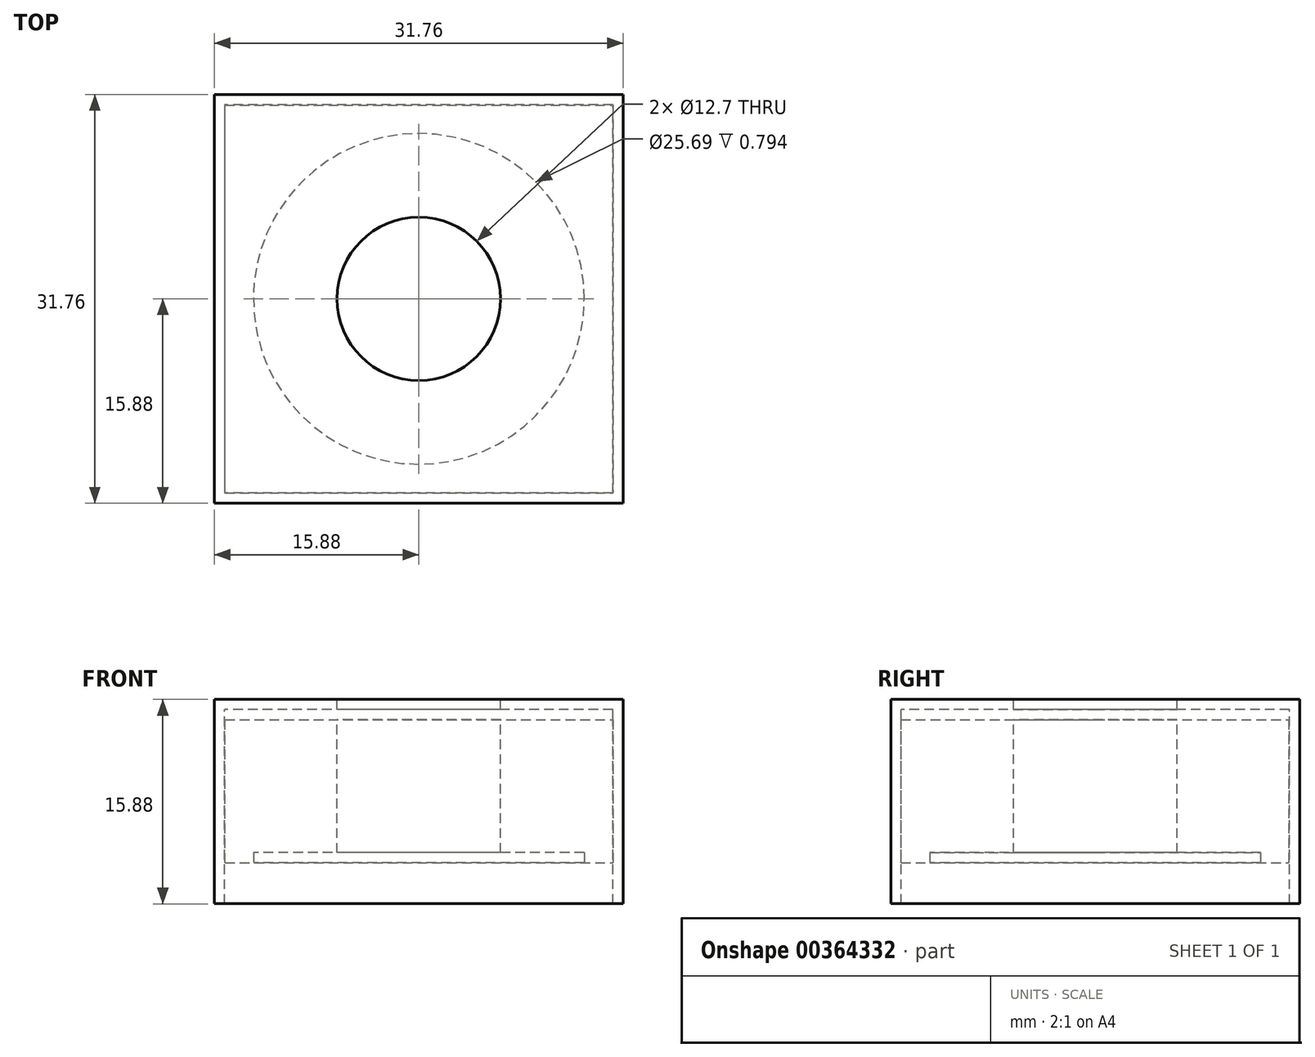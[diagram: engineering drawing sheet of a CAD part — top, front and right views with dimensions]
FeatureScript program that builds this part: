
annotation { "Feature Type Name" : "Feature", "Feature Type Description" : "" }
export const myFeature = defineFeature(function(context is Context, id is Id, definition is map)
    precondition{}
    {
        {
            var Q0;
            Q0=qCreatedBy(makeId("Top.planeOp"),FACE);
            var sketch = newSketch(context, id + "F0", { "sketchPlane" : qUnion([Q0])});
            skLineSegment(sketch, "E0.bottom", {"start": v(15.87, 15.88) * mm, "end": v(-15.88, 15.88) * mm});
            skLineSegment(sketch, "E0.top", {"start": v(15.88, -15.87) * mm, "end": v(-15.87, -15.87) * mm});
            skLineSegment(sketch, "E0.left", {"start": v(15.87, 15.88) * mm, "end": v(15.88, -15.87) * mm});
            skLineSegment(sketch, "E0.right", {"start": v(-15.88, 15.88) * mm, "end": v(-15.87, -15.87) * mm});
            skPoint(sketch, "E0.middle", {"position": v(0, 0) * mm});
            skSolve(sketch);
        }
        {
            var Q0;
            Q0 = qSketchRegion(id + "F0", true);
            extrude(context, id + "F1", {"entities" : qUnion([Q0]), "oppositeDirection" : true, "depth" : 15.88 * mm});
        }
        {
            var Q0;
            Q0=makeQuery(id+"F1.opExtrude","CAP_FACE",FACE,{"disambiguationData":[OSD([sQuery(id+"F0.wireOp",EDGE,"E0.bottom"),sQuery(id+"F0.wireOp",EDGE,"E0.top"),sQuery(id+"F0.wireOp",EDGE,"E0.left"),sQuery(id+"F0.wireOp",EDGE,"E0.right")])],"isStart":false});
            shell(context, id + "F2", {"entities" : qUnion([Q0]), "thickness" : 0.8 * mm});
        }
        {
            var Q0;
            Q0=qCreatedBy(makeId("Top.planeOp"),FACE);
            cPlane(context, id + "F3", {"entities" : qUnion([Q0]), "cplaneType" : CPlaneType.OFFSET, "offset" : 12.7 * mm, "oppositeDirection" : true, "width" : 152.4 * mm, "height" : 152.4 * mm});
        }
        {
            var Q0;
            Q0=qCreatedBy(id+"F3.planeOp",FACE);
            var sketch = newSketch(context, id + "F4", { "sketchPlane" : qUnion([Q0])});
            skLineSegment(sketch, "E1.bottom", {"start": v(-15.05, -15.08) * mm, "end": v(15.17, -15.08) * mm});
            skLineSegment(sketch, "E1.top", {"start": v(-15.05, 15.04) * mm, "end": v(15.17, 15.04) * mm});
            skLineSegment(sketch, "E1.left", {"start": v(-15.05, -15.08) * mm, "end": v(-15.05, 15.04) * mm});
            skLineSegment(sketch, "E1.right", {"start": v(15.17, -15.08) * mm, "end": v(15.17, 15.04) * mm});
            skSolve(sketch);
        }
        {
            var Q0;
            Q0 = qSketchRegion(id + "F4", true);
            extrude(context, id + "F5", {"entities" : qUnion([Q0]), "operationType" : NewBodyOperationType.ADD, "depth" : 11.1 * mm});
        }
        {
            var Q0;
            Q0=makeQuery(id+"F1.opExtrude","CAP_FACE",FACE,{"disambiguationData":[OSD([sQuery(id+"F0.wireOp",EDGE,"E0.bottom"),sQuery(id+"F0.wireOp",EDGE,"E0.top"),sQuery(id+"F0.wireOp",EDGE,"E0.left"),sQuery(id+"F0.wireOp",EDGE,"E0.right")])],"isStart":true});
            var sketch = newSketch(context, id + "F6", { "sketchPlane" : qUnion([Q0])});
            skCircle(sketch, "E2", {"center": v(0, 0) * mm, "radius": 6.35 * mm});
            skSolve(sketch);
        }
        {
            var Q0;
            Q0 = qSketchRegion(id + "F6", true);
            extrude(context, id + "F7", {"entities" : qUnion([Q0]), "operationType" : NewBodyOperationType.REMOVE, "endBound" : BoundingType.THROUGH_ALL, "oppositeDirection" : true, "depth" : 25.4 * mm});
        }
        {
            var Q0;
            Q0=qCreatedBy(id+"F3.planeOp",FACE);
            var sketch = newSketch(context, id + "F8", { "sketchPlane" : qUnion([Q0])});
            skCircle(sketch, "E3", {"center": v(0, 0) * mm, "radius": 12.85 * mm});
            skSolve(sketch);
        }
        {
            var Q0;
            Q0 = qSketchRegion(id + "F8", true);
            extrude(context, id + "F9", {"entities" : qUnion([Q0]), "operationType" : NewBodyOperationType.REMOVE, "depth" : 0.8 * mm});
        }
    });
